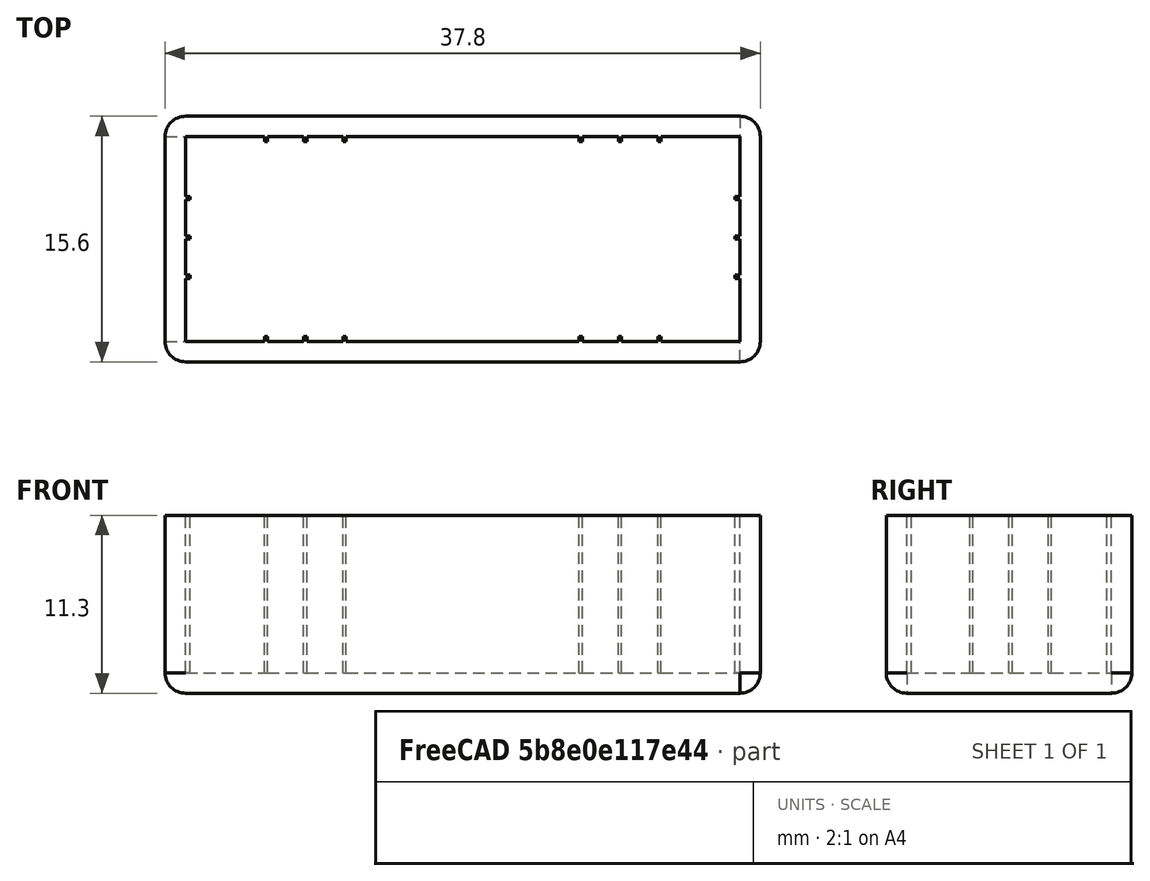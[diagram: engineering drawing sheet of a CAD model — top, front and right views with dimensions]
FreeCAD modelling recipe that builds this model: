
FCSTD DOCUMENT  (FreeCAD 0.18RUnknown)
Label: Tapa Bateria
License: All rights reserved
LicenseURL: http://en.wikipedia.org/wiki/All_rights_reserved
objects: Part::FeaturePython×4, Part::Box×2, App::MeasureDistance×2, Part::Thickness×1, Part::MultiFuse×1
note: 8 computed .brp shape members not serialized (recipe doc carries the construction recipe); baked Part::Feature solids carry a one-line shape summary decoded from their .brp

FEATURE [Part::Box] Box  label="Cubo"
  AttacherType = Attacher::AttachEngine3D
  Height = 10
  Length = 35.2
  Width = 13
FEATURE [Part::Thickness] Thickness
  Faces = -> Box [Face6]
  Intersection = false
  Join = 0
  Mode = 0
  SelfIntersection = false
  Value = 1.3
FEATURE [Part::Box] Box001  label="Cubo001"
  AttacherType = Attacher::AttachEngine3D
  Height = 10
  Length = 0.2
  Placement = pos=(5,0,0) rot=(0,0,1;0rad)
  Width = 0.3
FEATURE [Part::FeaturePython] Array  # Draft array (typed FeaturePython)
  Angle = 360
  ArrayType = 0
  Axis = (0,0,1)
  Base = -> Box001
  Center = (0,0,0)
  Fuse = false
  IntervalAxis = (0,0,0)
  IntervalX = (2.5,0,0)
  IntervalY = (0,1,0)
  IntervalZ = (0,0,1)
  NumberPolar = 1
  NumberX = 3
  NumberY = 1
  NumberZ = 1
FEATURE [Part::FeaturePython] Array001  label="trabas h"  # Draft array (typed FeaturePython)
  Angle = 360
  ArrayType = 0
  Axis = (0,0,1)
  Base = -> Array
  Center = (0,0,0)
  Fuse = false
  IntervalAxis = (0,0,0)
  IntervalX = (20,0,0)
  IntervalY = (0,12.7,0)
  IntervalZ = (0,0,1)
  NumberPolar = 1
  NumberX = 2
  NumberY = 2
  NumberZ = 1
FEATURE [Part::FeaturePython] Clone  label="Array002"  # Draft clone (typed FeaturePython)
  AttacherType = Attacher::AttachEngine3D
  Fuse = false
  Objects = -> [Array]
  Placement = pos=(0.3,-1,0) rot=(0,0,1;1.5708rad)
  Scale = (1,1,1)
FEATURE [Part::FeaturePython] Array002  label="Travas v"  # Draft array (typed FeaturePython)
  Angle = 360
  ArrayType = 0
  Axis = (0,0,1)
  Base = -> Clone
  Center = (0,0,0)
  Fuse = false
  IntervalAxis = (0,0,0)
  IntervalX = (34.9,0,0)
  IntervalY = (0,1,0)
  IntervalZ = (0,0,1)
  NumberPolar = 1
  NumberX = 2
  NumberY = 0
  NumberZ = 1
FEATURE [Part::MultiFuse] Fusion  label="Tapa"
  Shapes = -> [Thickness,Array001,Array002]
FEATURE [App::MeasureDistance] Distance  label="Distance: 13,05 mm"
  Distance = 13.0499
  P1 = (14.7264,-0.00825163,10)
  P2 = (15.7677,13,10)
FEATURE [App::MeasureDistance] Distance001  label="Distance: 35,21 mm"
  Distance = 35.2081
  P1 = (35.2,2.62123,10)
  P2 = (5e-16,1.86561,10)
